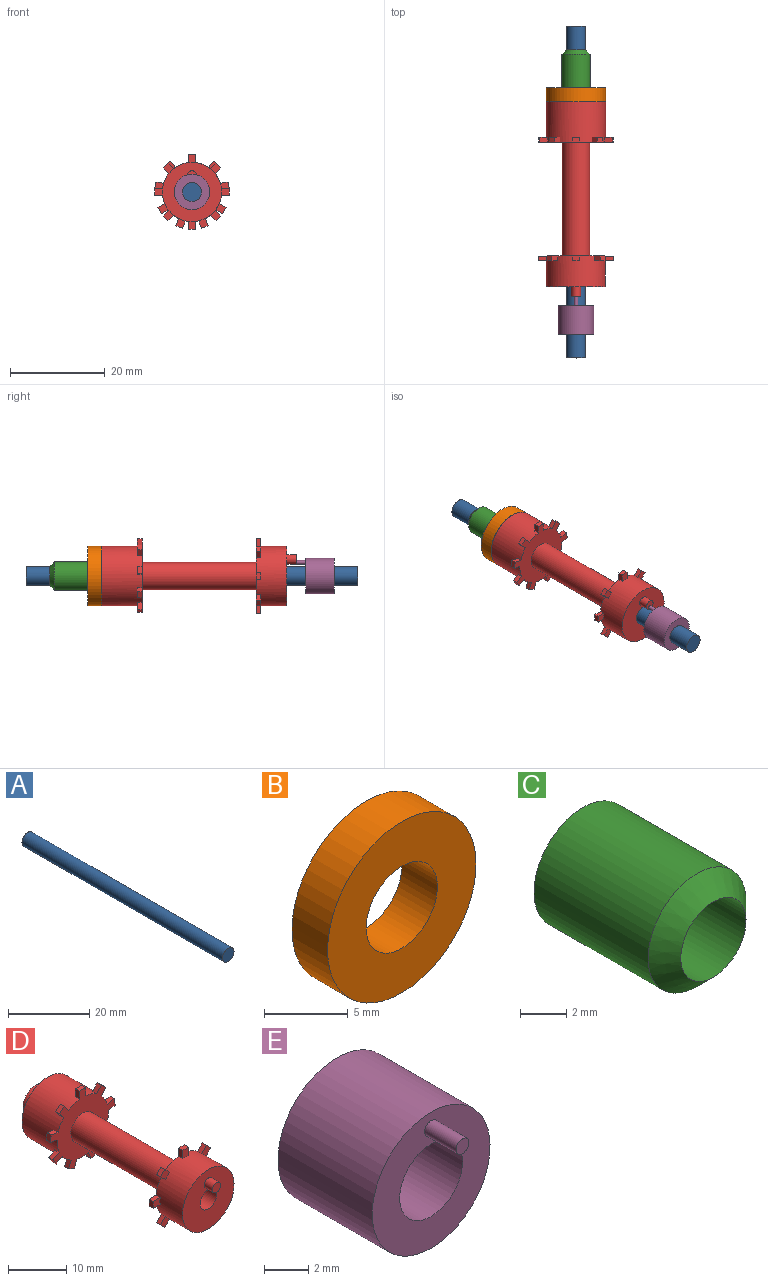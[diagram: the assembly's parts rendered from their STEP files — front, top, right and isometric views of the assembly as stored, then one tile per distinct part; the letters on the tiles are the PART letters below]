
ASSEMBLY  parts=5 mates=4
PART A: 3 faces, bbox 4x70x4 mm
  f0: cylinder r=2mm len=70mm, axis (0,1,0), area 879.6mm2, adj f1,f2
  f1: plane 4x4mm, normal (0,-1,0), area 12.6mm2, adj f0
  f2: plane 4x4mm, normal (0,1,0), area 12.6mm2, adj f0
PART B: 4 faces, bbox 12.5x3x12.5 mm
  f0: cylinder r=3mm len=6mm, axis (0,1,0), area 56.5mm2, adj f2,f3
  f1: cylinder r=6.25mm len=12.5mm, axis (0,1,0), area 117.8mm2, adj f2,f3
  f2: plane 12.5x12.5mm, normal (0,-1,0), area 94.4mm2, adj f0,f1
  f3: plane 12.5x12.5mm, normal (0,1,0), area 94.4mm2, adj f0,f1
PART C: 4 faces, bbox 6x8x6 mm
  f0: cylinder r=2mm len=8mm, axis (0,1,0), area 100.5mm2, adj f2,f3
  f1: cylinder r=3mm len=7mm, axis (0,1,0), area 131.9mm2, adj f2,f3
  f2: plane 6x6mm, normal (0,1,0), area 15.7mm2, adj f0,f1
  f3: cone r=2mm half-angle=45deg, axis (0,1,0), area 22.2mm2, adj f0,f1
PART D: 81 faces, bbox 15.8x44x15.8 mm
  f0: cylinder r=6.25mm len=12.5mm, axis (0,1,0), area 320.3mm2, adj f1,f2,f3,f5,f44,f45,f46,f48
  f1: plane 15.78x15.54mm, normal (0,-1,0), area 118.7mm2, adj f0,f2,f3,f4,f13,f43,f45,f46
  f2: plane 1.45x1mm, normal (-0.5,0,-0.87), area 1.7mm2, adj f0,f1,f4,f5
  f3: plane 1.45x1mm, normal (0.5,0,0.87), area 1.7mm2, adj f0,f1,f4,f5
  f4: plane 1.3x1mm, normal (0.87,0,-0.5), area 1.5mm2, adj f1,f2,f3,f5
  f5: plane 2.2x2.14mm, normal (0,1,0), area 2.5mm2, adj f0,f2,f3,f4
  f6: plane 2.22x2.22mm, normal (0,-1,0), area 2.4mm2, adj f15,f22,f23,f24
  f7: plane 1.69x1.45mm, normal (0,-1,0), area 2.4mm2, adj f15,f25,f26,f27
  f8: plane 2.22x2.22mm, normal (0,-1,0), area 2.4mm2, adj f15,f28,f29,f30
  f9: plane 1.69x1.45mm, normal (0,-1,0), area 2.4mm2, adj f15,f31,f32,f33
  f10: plane 2.22x2.22mm, normal (0,-1,0), area 2.4mm2, adj f15,f34,f35,f36
  f11: plane 1.69x1.45mm, normal (0,-1,0), area 2.4mm2, adj f14,f15,f37,f38
  f12: plane 1.69x1.45mm, normal (0,-1,0), area 2.4mm2, adj f19,f20,f21,f41
  f13: cylinder r=2.89mm len=24mm, axis (0,1,0), area 436mm2, adj f1,f40
  f14: plane 1.69x1mm, normal (1,0,0), area 1.7mm2, adj f11,f15,f38,f40
  f15: cylinder r=6.25mm len=12.5mm, axis (0,1,0), area 235.6mm2, adj f6,f7,f8,f9,f10,f11,f14,f16
  f16: plane 1.19x1.19mm, normal (-0.71,0,-0.71), area 1.7mm2, adj f15,f17,f39,f40
  f17: plane 1.03x1.03mm, normal (0.71,0,-0.71), area 1.4mm2, adj f16,f18,f39,f40
  f18: plane 1.19x1.19mm, normal (0.71,0,0.71), area 1.7mm2, adj f15,f17,f39,f40
  f19: plane 1.69x1mm, normal (0,0,-1), area 1.7mm2, adj f12,f15,f20,f40
  f20: plane 1.45x1mm, normal (1,0,0), area 1.4mm2, adj f12,f19,f21,f40
  f21: plane 1.69x1mm, normal (0,0,1), area 1.7mm2, adj f12,f15,f20,f40
  f22: plane 1.19x1.19mm, normal (0.71,0,-0.71), area 1.7mm2, adj f6,f15,f23,f40
  f23: plane 1.03x1.03mm, normal (0.71,0,0.71), area 1.4mm2, adj f6,f22,f24,f40
  f24: plane 1.19x1.19mm, normal (-0.71,0,0.71), area 1.7mm2, adj f6,f15,f23,f40
  f25: plane 1.69x1mm, normal (1,0,0), area 1.7mm2, adj f7,f15,f26,f40
  f26: plane 1.45x1mm, normal (0,0,1), area 1.4mm2, adj f7,f25,f27,f40
  f27: plane 1.69x1mm, normal (-1,0,0), area 1.7mm2, adj f7,f15,f26,f40
  f28: plane 1.19x1.19mm, normal (0.71,0,0.71), area 1.7mm2, adj f8,f15,f29,f40
  f29: plane 1.03x1.03mm, normal (-0.71,0,0.71), area 1.4mm2, adj f8,f28,f30,f40
  f30: plane 1.19x1.19mm, normal (-0.71,0,-0.71), area 1.7mm2, adj f8,f15,f29,f40
  f31: plane 1.69x1mm, normal (0,0,1), area 1.7mm2, adj f9,f15,f32,f40
  f32: plane 1.45x1mm, normal (-1,0,0), area 1.4mm2, adj f9,f31,f33,f40
  f33: plane 1.69x1mm, normal (0,0,-1), area 1.7mm2, adj f9,f15,f32,f40
  f34: plane 1.19x1.19mm, normal (-0.71,0,0.71), area 1.7mm2, adj f10,f15,f35,f40
  f35: plane 1.03x1.03mm, normal (-0.71,0,-0.71), area 1.4mm2, adj f10,f34,f36,f40
  f36: plane 1.19x1.19mm, normal (0.71,0,-0.71), area 1.7mm2, adj f10,f15,f35,f40
  f37: plane 1.69x1mm, normal (-1,0,0), area 1.7mm2, adj f11,f15,f38,f40
  f38: plane 1.45x1mm, normal (0,0,-1), area 1.4mm2, adj f11,f14,f37,f40
  f39: plane 2.22x2.22mm, normal (0,-1,0), area 2.4mm2, adj f15,f16,f17,f18
  f40: plane 15.79x15.79mm, normal (0,1,0), area 115.7mm2, adj f13,f14,f15,f16,f17,f18,f19,f20
  f41: extruded ~5.5x1.45mm, area 8mm2, adj f12,f15,f78
  f42: cylinder r=2mm len=42mm, axis (0,-1,0), area 527.8mm2, adj f77,f78
  f43: plane 1.48x1mm, normal (0.98,0,0.17), area 1.5mm2, adj f1,f44,f45,f46
  f44: plane 1.91x1.77mm, normal (0,1,0), area 2.5mm2, adj f0,f43,f45,f46
  f45: plane 1.65x1mm, normal (-0.17,0,0.98), area 1.7mm2, adj f0,f1,f43,f44
  f46: plane 1.65x1mm, normal (0.17,0,-0.98), area 1.7mm2, adj f0,f1,f43,f44
  f47: plane 1.41x1mm, normal (-0.34,0,-0.94), area 1.5mm2, adj f1,f48,f49,f50
  f48: plane 2.09x1.98mm, normal (0,1,0), area 2.5mm2, adj f0,f47,f49,f50
  f49: plane 1.58x1mm, normal (-0.94,0,0.34), area 1.7mm2, adj f0,f1,f47,f48
  f50: plane 1.58x1mm, normal (0.94,0,-0.34), area 1.7mm2, adj f0,f1,f47,f48
  f51: plane 1.15x1mm, normal (0.64,0,0.77), area 1.5mm2, adj f1,f52,f53,f54
  f52: plane 2.25x2.23mm, normal (0,1,0), area 2.5mm2, adj f0,f51,f53,f54
  f53: plane 1.28x1.08mm, normal (0.77,0,-0.64), area 1.7mm2, adj f0,f1,f51,f52
  f54: plane 1.28x1.08mm, normal (-0.77,0,0.64), area 1.7mm2, adj f0,f1,f51,f52
  f55: plane 1.15x1mm, normal (-0.64,0,0.77), area 1.5mm2, adj f1,f56,f57,f58
  f56: plane 1.28x1.08mm, normal (-0.77,0,-0.64), area 1.7mm2, adj f0,f1,f55,f58
  f57: plane 1.28x1.08mm, normal (0.77,0,0.64), area 1.7mm2, adj f0,f1,f55,f58
  f58: plane 2.25x2.23mm, normal (0,1,0), area 2.5mm2, adj f0,f55,f56,f57
  f59: plane 1.48x1mm, normal (-0.98,0,0.17), area 1.5mm2, adj f1,f60,f61,f62
  f60: plane 1.65x1mm, normal (-0.17,0,-0.98), area 1.7mm2, adj f0,f1,f59,f62
  f61: plane 1.65x1mm, normal (0.17,0,0.98), area 1.7mm2, adj f0,f1,f59,f62
  f62: plane 1.91x1.77mm, normal (0,1,0), area 2.5mm2, adj f0,f59,f60,f61
  f63: plane 1.41x1mm, normal (0.34,0,-0.94), area 1.5mm2, adj f1,f64,f65,f66
  f64: plane 1.58x1mm, normal (0.94,0,0.34), area 1.7mm2, adj f0,f1,f63,f66
  f65: plane 1.58x1mm, normal (-0.94,0,-0.34), area 1.7mm2, adj f0,f1,f63,f66
  f66: plane 2.09x1.98mm, normal (0,1,0), area 2.5mm2, adj f0,f63,f64,f65
  f67: plane 1.5x1mm, normal (0,0,1), area 1.5mm2, adj f1,f68,f69,f70
  f68: plane 1.68x1mm, normal (-1,0,0), area 1.7mm2, adj f0,f1,f67,f70
  f69: plane 1.68x1mm, normal (1,0,0), area 1.7mm2, adj f0,f1,f67,f70
  f70: plane 1.68x1.5mm, normal (0,1,0), area 2.5mm2, adj f0,f67,f68,f69
  f71: plane 1.45x1mm, normal (-0.5,0,0.87), area 1.7mm2, adj f0,f1,f73,f74
  f72: plane 1.45x1mm, normal (0.5,0,-0.87), area 1.7mm2, adj f0,f1,f73,f74
  f73: plane 1.3x1mm, normal (-0.87,0,-0.5), area 1.5mm2, adj f1,f71,f72,f74
  f74: plane 2.2x2.14mm, normal (0,1,0), area 2.5mm2, adj f0,f71,f72,f73
  f75: plane 12.5x12.5mm, normal (0,1,0), area 94.4mm2, adj f0,f76
  f76: cylinder r=3mm len=6mm, axis (0,-1,0), area 56.5mm2, adj f75,f77
  f77: plane 6x6mm, normal (0,1,0), area 15.7mm2, adj f42,f76
  f78: plane 12.5x12.5mm, normal (0,-1,0), area 107mm2, adj f15,f41,f42,f79
  f79: cylinder r=1mm len=2mm, axis (0,1,0), area 12.6mm2, adj f78,f80
  f80: plane 2x2mm, normal (0,-1,0), area 3.1mm2, adj f79
PART E: 6 faces, bbox 7.5x8x7.5 mm
  f0: cylinder r=2mm len=6mm, axis (0,1,0), area 75.4mm2, adj f2,f3
  f1: cylinder r=3.75mm len=7.5mm, axis (0,1,0), area 141.4mm2, adj f2,f3
  f2: plane 7.5x7.5mm, normal (0,-1,0), area 31.1mm2, adj f0,f1,f4
  f3: plane 7.5x7.5mm, normal (0,1,0), area 31.6mm2, adj f0,f1
  f4: cylinder r=0.41mm len=2mm, axis (0,1,0), area 5.1mm2, adj f2,f5
  f5: plane 0.82x0.82mm, normal (0,-1,0), area 0.5mm2, adj f4
PLACE A rot(axis=(0,-1,0),0deg) t=(-27.72,15.18,-12.79)mm
PLACE B rot(axis=(0,-1,0),0deg) t=(-27.72,2.18,-12.79)mm
PLACE C rot(axis=(-1,0,0),180deg) t=(-27.72,2.18,-12.79)mm
PLACE D t=(-27.72,-3.32,-12.79)mm
PLACE E rot(axis=(0,0,-1),180deg) t=(-27.72,-49.82,-12.79)mm
MATE fastened C.f0 <-> A.f0  axis (0,-1,0) through (-27.72,2.18,-12.79)mm
MATE fastened B.f1 <-> D.f0  axis (0,-1,0) through (-27.72,-0.82,-12.79)mm
MATE cylindrical B.f1 <-> A.f0  axis (0,1,0) through (-27.72,2.18,-12.79)mm
MATE fastened A.f0 <-> E.f0  axis (0,-1,0) through (-27.72,-54.82,-12.79)mm
